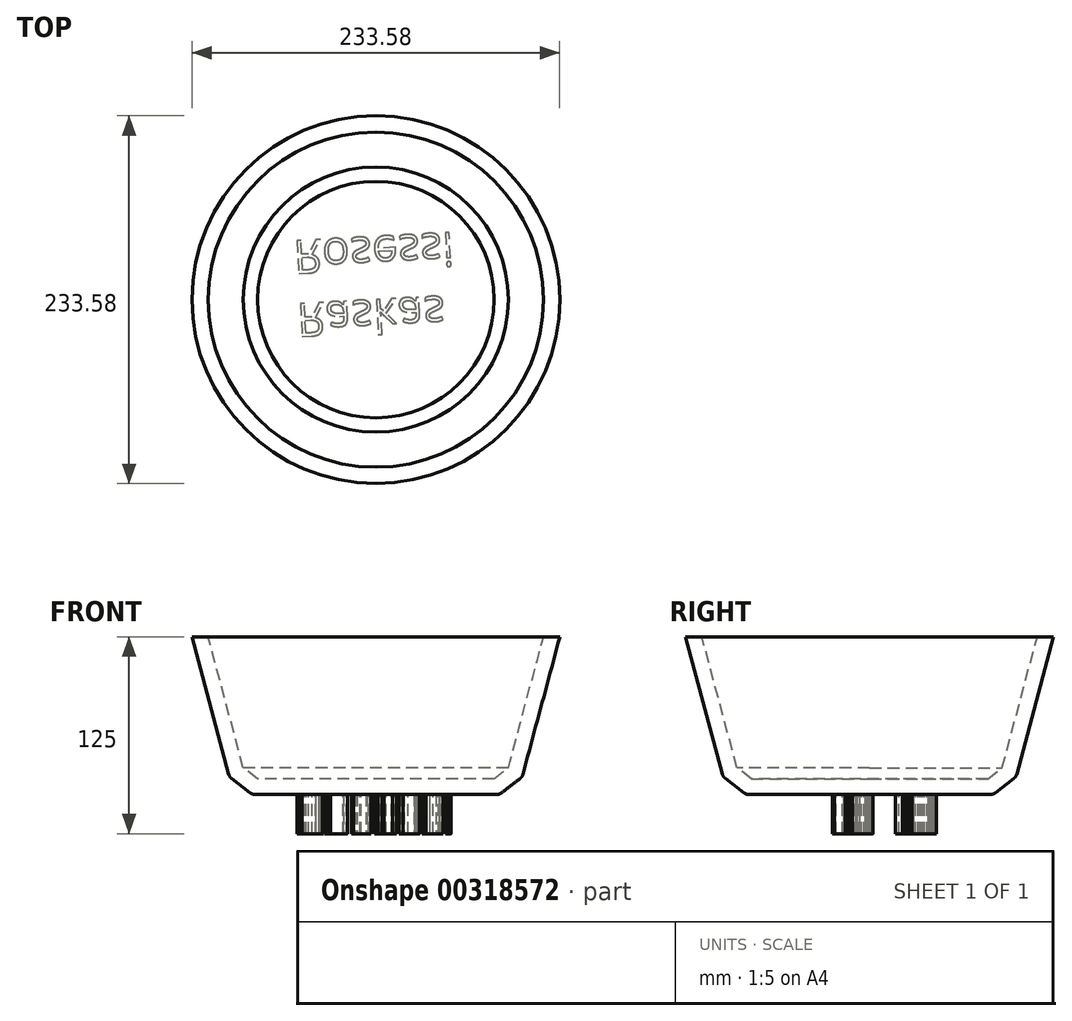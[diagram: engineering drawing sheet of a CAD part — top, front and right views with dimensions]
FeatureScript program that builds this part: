
annotation { "Feature Type Name" : "Feature", "Feature Type Description" : "" }
export const myFeature = defineFeature(function(context is Context, id is Id, definition is map)
    precondition{}
    {
        {
            var Q0;
            Q0=qCreatedBy(makeId("Top.planeOp"),FACE);
            var sketch = newSketch(context, id + "F0", { "sketchPlane" : qUnion([Q0])});
            skCircle(sketch, "E0", {"center": v(0, 0) * mm, "radius": 90 * mm});
            skSolve(sketch);
        }
        {
            var Q0;
            Q0=makeQuery(id+"F0.imprint","IMPRINT",FACE,{"disambiguationData":[TD([[makeQuery(id+"F0.imprint","IMPRINT",EDGE,{"derivedFrom":sQuery(id+"F0.wireOp",EDGE,"E0")}),1.0]])]});
            extrude(context, id + "F1", {"entities" : qUnion([Q0]), "depth" : 100 * mm, "hasDraft" : true, "draftAngle" : 15 * degree});
        }
        {
            var Q0;
            Q0=makeQuery(id+"F1.opExtrude","CAP_EDGE",EDGE,{"disambiguationData":[OSD([sQuery(id+"F0.wireOp",EDGE,"E0")])],"isStart":true});
            chamfer(context, id + "F2", {"entities" : qUnion([Q0]), "width" : 15 * mm, "tangentPropagation" : true});
        }
        {
            var Q0;
            {var subQ0=sQuery(id+"F0.wireOp",EDGE,"E0");Q0=makeQuery(id+"F2.opChamfer","BLEND_EDGE",EDGE,{"blendedFrom":[makeQuery(id+"F1.opExtrude","CAP_EDGE",EDGE,{"disambiguationData":[OSD([subQ0])],"isStart":true}),makeQuery(id+"F1.opExtrude","SWEPT_FACE",FACE,{"disambiguationData":[OSD([subQ0])]})],"blendedInto":[makeQuery(id+"F1.opExtrude","SWEPT_FACE",FACE,{"disambiguationData":[OSD([subQ0])]})]});}
            var Q1;
            {var subQ0=sQuery(id+"F0.wireOp",EDGE,"E0");Q1=makeQuery(id+"F2.opChamfer","BLEND_EDGE",EDGE,{"blendedFrom":[makeQuery(id+"F1.opExtrude","CAP_EDGE",EDGE,{"disambiguationData":[OSD([subQ0])],"isStart":true}),makeQuery(id+"F1.opExtrude","CAP_FACE",FACE,{"disambiguationData":[OSD([subQ0])],"isStart":true})],"blendedInto":[makeQuery(id+"F1.opExtrude","CAP_FACE",FACE,{"disambiguationData":[OSD([subQ0])],"isStart":true})]});}
            fillet(context, id + "F3", {"entities" : qUnion([Q0, Q1]), "radius" : 5 * mm, "tangentPropagation" : true, "allowEdgeOverflow" : false});
        }
        {
            var Q0;
            Q0=makeQuery(id+"F1.opExtrude","CAP_FACE",FACE,{"disambiguationData":[OSD([sQuery(id+"F0.wireOp",EDGE,"E0")])],"isStart":false});
            shell(context, id + "F4", {"entities" : qUnion([Q0]), "thickness" : 10 * mm});
        }
        {
            var Q0;
            Q0=makeQuery(id+"F1.opExtrude","CAP_FACE",FACE,{"disambiguationData":[OSD([sQuery(id+"F0.wireOp",EDGE,"E0")])],"isStart":true});
            var sketch = newSketch(context, id + "F5", { "sketchPlane" : qUnion([Q0])});
            skText(sketch, "E1", { "text": "Raskas\nRosessi", "fontName": "OpenSans-Regular.ttf"});
            const initialGuessF5  = {"E1": [-0.05074, 0.00271, 0.99857, -0.0534, 0.02119]};
            skSetInitialGuess(sketch, initialGuessF5);
            skSolve(sketch);
        }
        {
            var Q0;
            Q0=qSketchRegion(id+"F5",true);
            extrude(context, id + "F6", {"entities" : qUnion([Q0]), "operationType" : NewBodyOperationType.ADD, "depth" : 25 * mm});
        }
        {
            var Q0;
            Q0=qCreatedBy(makeId("Front.planeOp"),FACE);
            var sketch = newSketch(context, id + "F7", { "sketchPlane" : qUnion([Q0])});
            skFitSpline(sketch, "E2", {"points": [v(-208.5, 107.86) * mm, v(-201.07, 73.66) * mm, v(-219.66, 35.63) * mm, v(-251.05, 11.92) * mm, v(-267.53, -15.26) * mm, v(-269.18, -72.57) * mm, v(-261.45, -122.25) * mm, v(-229.04, -124.13) * mm, v(-236.8, -134.04) * mm, v(-289.54, -142.74) * mm], "startDerivative": vector(118.52, -311.62) * mm, "endDerivative": vector(-462.2, -19.06) * mm});
            skLineSegment(sketch, "E3", {"start": v(-341.4, 142.15) * mm, "end": v(-341.4, -175.75) * mm});
            skSolve(sketch);
        }
        {
            var Q0;
            Q0 = qSketchRegion(id + "F7", true);
            var Q1;
            Q1=sQuery(id+"F7.wireOp",EDGE,"E2");
            var Q2;
            Q2=sQuery(id+"F7.wireOp",EDGE,"E3");
            revolve(context, id + "F8", {"bodyType" : ToolBodyType.SURFACE, "entities" : qUnion([Q0]), "surfaceEntities" : qUnion([Q1]), "axis" : qUnion([Q2]), "revolveType" : RevolveType.FULL});
        }
    });
